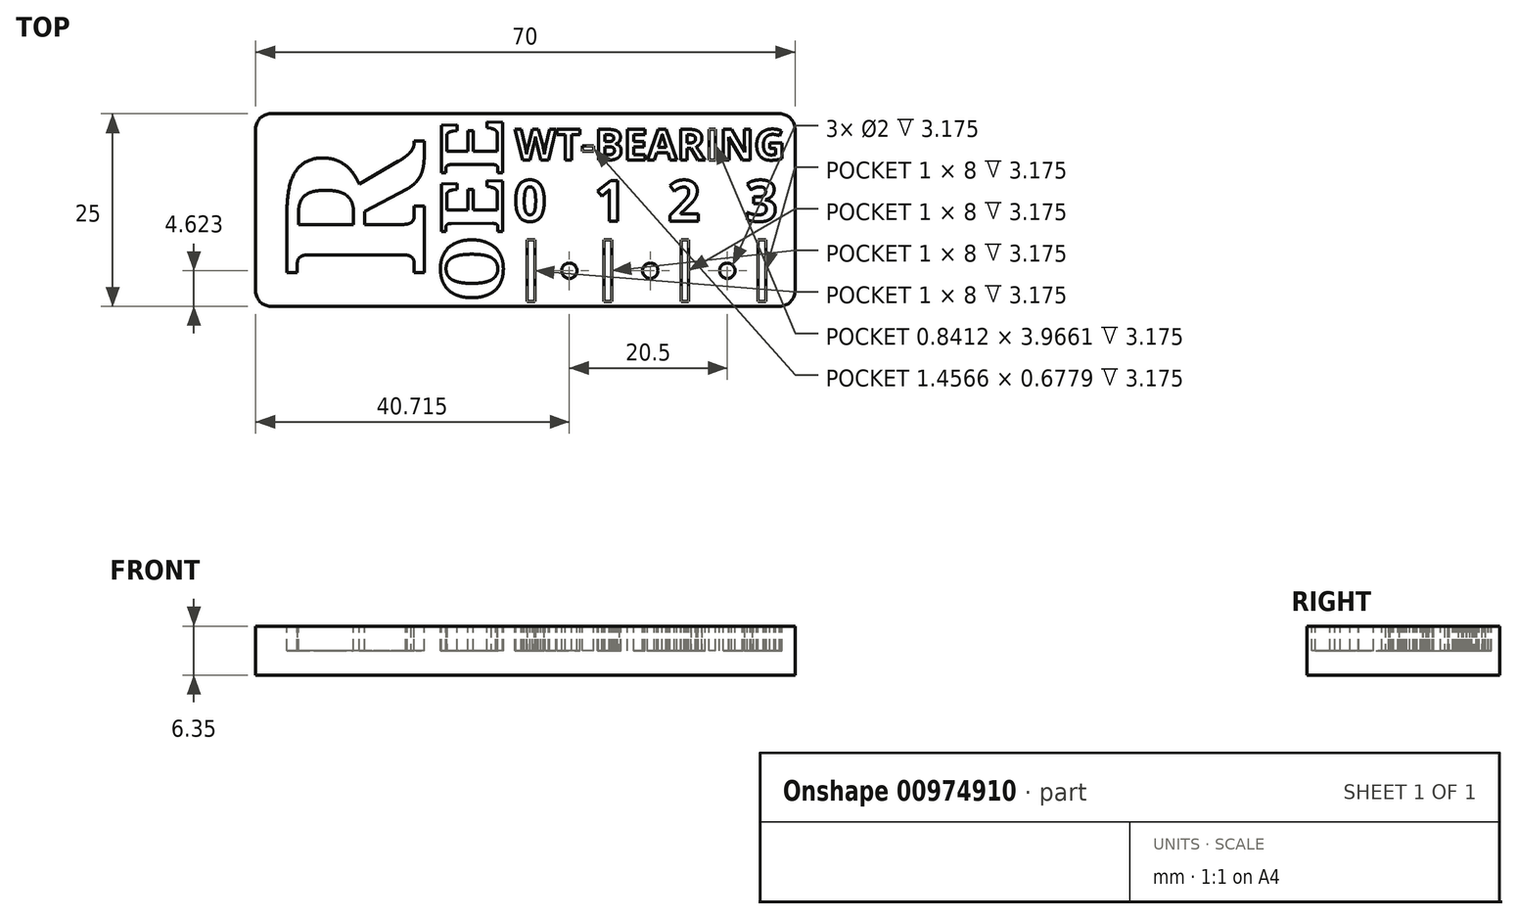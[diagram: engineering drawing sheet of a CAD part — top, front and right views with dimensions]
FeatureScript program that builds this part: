
annotation { "Feature Type Name" : "Feature", "Feature Type Description" : "" }
export const myFeature = defineFeature(function(context is Context, id is Id, definition is map)
    precondition{}
    {
        {
            var Q0;
            Q0=qCreatedBy(makeId("Top.planeOp"),FACE);
            var sketch = newSketch(context, id + "F0", { "sketchPlane" : qUnion([Q0])});
            skLineSegment(sketch, "E0.bottom", {"start": v(-55.27, 9.73) * mm, "end": v(10.73, 9.73) * mm});
            skLineSegment(sketch, "E0.top", {"start": v(-55.27, -15.27) * mm, "end": v(10.73, -15.27) * mm});
            skLineSegment(sketch, "E0.left", {"start": v(-57.27, 7.73) * mm, "end": v(-57.27, -13.27) * mm});
            skLineSegment(sketch, "E0.right", {"start": v(12.73, 7.73) * mm, "end": v(12.73, -13.27) * mm});
            skPoint(sketch, "E1.visualSharp", {"position": v(-57.27, 9.73) * mm});
            skArc(sketch, "E1.filletArc", {"start": v(-55.27, 9.73) * mm, "mid": v(-56.68, 9.15) * mm, "end": v(-57.27, 7.73) * mm});
            skPoint(sketch, "E2.visualSharp", {"position": v(12.73, 9.73) * mm});
            skArc(sketch, "E2.filletArc", {"start": v(12.73, 7.73) * mm, "mid": v(12.14, 9.15) * mm, "end": v(10.73, 9.73) * mm});
            skPoint(sketch, "E3.visualSharp", {"position": v(12.73, -15.27) * mm});
            skArc(sketch, "E3.filletArc", {"start": v(10.73, -15.27) * mm, "mid": v(12.14, -14.68) * mm, "end": v(12.73, -13.27) * mm});
            skPoint(sketch, "E4.visualSharp", {"position": v(-57.27, -15.27) * mm});
            skArc(sketch, "E4.filletArc", {"start": v(-57.27, -13.27) * mm, "mid": v(-56.68, -14.68) * mm, "end": v(-55.27, -15.27) * mm});
            skSolve(sketch);
        }
        {
            var Q0;
            Q0=qSketchRegion(id+"F0",true);
            extrude(context, id + "F1", {"entities" : qUnion([Q0]), "depth" : 6.35 * mm, "offsetDistance" : 25.4 * mm});
        }
        {
            var Q0;
            Q0=makeQuery(id+"F1.opExtrude","CAP_FACE",FACE,{"disambiguationData":[OSD([sQuery(id+"F0.wireOp",EDGE,"E0.bottom"),sQuery(id+"F0.wireOp",EDGE,"E0.top"),sQuery(id+"F0.wireOp",EDGE,"E0.left"),sQuery(id+"F0.wireOp",EDGE,"E0.right")])],"isStart":false});
            var sketch = newSketch(context, id + "F2", { "sketchPlane" : qUnion([Q0])});
            skText(sketch, "E5", { "text": "R", "fontName": "NotoSerif-Bold.ttf"});
            skText(sketch, "E6", { "text": "O\n", "fontName": "NotoSerif-Bold.ttf"});
            skText(sketch, "E7", { "text": "E", "fontName": "NotoSerif-Bold.ttf"});
            skLineSegment(sketch, "E8.bottom", {"start": v(-22.06, -6.65) * mm, "end": v(-21.06, -6.65) * mm});
            skLineSegment(sketch, "E8.top", {"start": v(-22.06, -14.65) * mm, "end": v(-21.06, -14.65) * mm});
            skLineSegment(sketch, "E8.left", {"start": v(-22.06, -6.65) * mm, "end": v(-22.06, -14.65) * mm});
            skLineSegment(sketch, "E8.right", {"start": v(-21.06, -6.65) * mm, "end": v(-21.06, -14.65) * mm});
            skLineSegment(sketch, "E9.bottom", {"start": v(-12.06, -6.65) * mm, "end": v(-11.06, -6.65) * mm});
            skLineSegment(sketch, "E9.top", {"start": v(-12.06, -14.65) * mm, "end": v(-11.06, -14.65) * mm});
            skLineSegment(sketch, "E9.left", {"start": v(-12.06, -6.65) * mm, "end": v(-12.06, -14.65) * mm});
            skLineSegment(sketch, "E9.right", {"start": v(-11.06, -6.65) * mm, "end": v(-11.06, -14.65) * mm});
            skLineSegment(sketch, "E10.bottom", {"start": v(-2.06, -6.65) * mm, "end": v(-1.06, -6.65) * mm});
            skLineSegment(sketch, "E10.top", {"start": v(-2.06, -14.65) * mm, "end": v(-1.06, -14.65) * mm});
            skLineSegment(sketch, "E10.left", {"start": v(-2.06, -6.65) * mm, "end": v(-2.06, -14.65) * mm});
            skLineSegment(sketch, "E10.right", {"start": v(-1.06, -6.65) * mm, "end": v(-1.06, -14.65) * mm});
            skLineSegment(sketch, "E11.bottom", {"start": v(7.94, -6.65) * mm, "end": v(8.94, -6.65) * mm});
            skLineSegment(sketch, "E11.top", {"start": v(7.94, -14.65) * mm, "end": v(8.94, -14.65) * mm});
            skLineSegment(sketch, "E11.left", {"start": v(7.94, -6.65) * mm, "end": v(7.94, -14.65) * mm});
            skLineSegment(sketch, "E11.right", {"start": v(8.94, -6.65) * mm, "end": v(8.94, -14.65) * mm});
            skPoint(sketch, "E12", {"position": v(-21.56, -6.65) * mm});
            skPoint(sketch, "E13", {"position": v(-11.56, -6.65) * mm});
            skPoint(sketch, "E14", {"position": v(-1.56, -6.65) * mm});
            skCircle(sketch, "E15", {"center": v(-16.56, -10.65) * mm, "radius": 1 * mm});
            skPoint(sketch, "E16", {"position": v(-21.06, -10.65) * mm});
            skCircle(sketch, "E17", {"center": v(-6.06, -10.65) * mm, "radius": 1 * mm});
            skCircle(sketch, "E18", {"center": v(3.94, -10.65) * mm, "radius": 1 * mm});
            skPoint(sketch, "E19", {"position": v(-11.06, -10.65) * mm});
            skPoint(sketch, "E20", {"position": v(-1.06, -10.65) * mm});
            skText(sketch, "E21", { "text": "0", "fontName": "OpenSans-Bold.ttf"});
            skText(sketch, "E22", { "text": "1", "fontName": "OpenSans-Bold.ttf"});
            skText(sketch, "E23", { "text": "2", "fontName": "OpenSans-Bold.ttf"});
            skText(sketch, "E24", { "text": "3", "fontName": "OpenSans-Bold.ttf"});
            skLineSegment(sketch, "E25", {"start": v(-39.23, 23.36) * mm, "end": v(-48.9, 23.36) * mm});
            skLineSegment(sketch, "E26", {"start": v(-48.9, 23.36) * mm, "end": v(-48.9, 20.36) * mm});
            skLineSegment(sketch, "E27", {"start": v(-48.9, 20.36) * mm, "end": v(-53.2, 24.99) * mm});
            skLineSegment(sketch, "E28", {"start": v(-53.2, 24.99) * mm, "end": v(-48.9, 28.97) * mm});
            skLineSegment(sketch, "E29", {"start": v(-48.9, 28.97) * mm, "end": v(-48.9, 25.97) * mm});
            skLineSegment(sketch, "E30", {"start": v(-48.9, 25.97) * mm, "end": v(-39.23, 25.97) * mm});
            skPoint(sketch, "E31", {"position": v(-41.72, 24.66) * mm});
            skLineSegment(sketch, "E32", {"start": v(-41.72, 24.66) * mm, "end": v(-39.23, 23.36) * mm});
            skLineSegment(sketch, "E33", {"start": v(-41.72, 24.66) * mm, "end": v(-39.23, 25.97) * mm});
            skText(sketch, "E34", { "text": "E", "fontName": "NotoSerif-Bold.ttf"});
            skText(sketch, "E35", { "text": "WT-BEARING", "fontName": "OpenSans-Bold.ttf"});
            const initialGuessF2  = {"E5": [-0.03535, -0.01161, 0, 1, 0.018], "E6": [-0.02523, -0.01477, 0, 1, 0.008], "E7": [-0.02523, -0.00585, -0.00042, 1, 0.008], "E21": [-0.02378, -0.00422, 1, 0, 0.00534], "E22": [-0.01333, -0.00422, 1, 0, 0.00534], "E23": [-0.0038, -0.00422, 1, 0, 0.00534], "E24": [0.00623, -0.00422, 1, 0, 0.00534], "E34": [-0.02523, 0.00178, -0.00042, 1, 0.008], "E35": [-0.02364, 0.00373, 1, 0, 0.004]};
            skSetInitialGuess(sketch, initialGuessF2);
            skSolve(sketch);
        }
        {
            var Q0;
            Q0=qSketchRegion(id+"F2",true);
            extrude(context, id + "F3", {"entities" : qUnion([Q0]), "operationType" : NewBodyOperationType.REMOVE, "oppositeDirection" : true, "depth" : 3.17 * mm, "offsetDistance" : 25.4 * mm});
        }
    });
